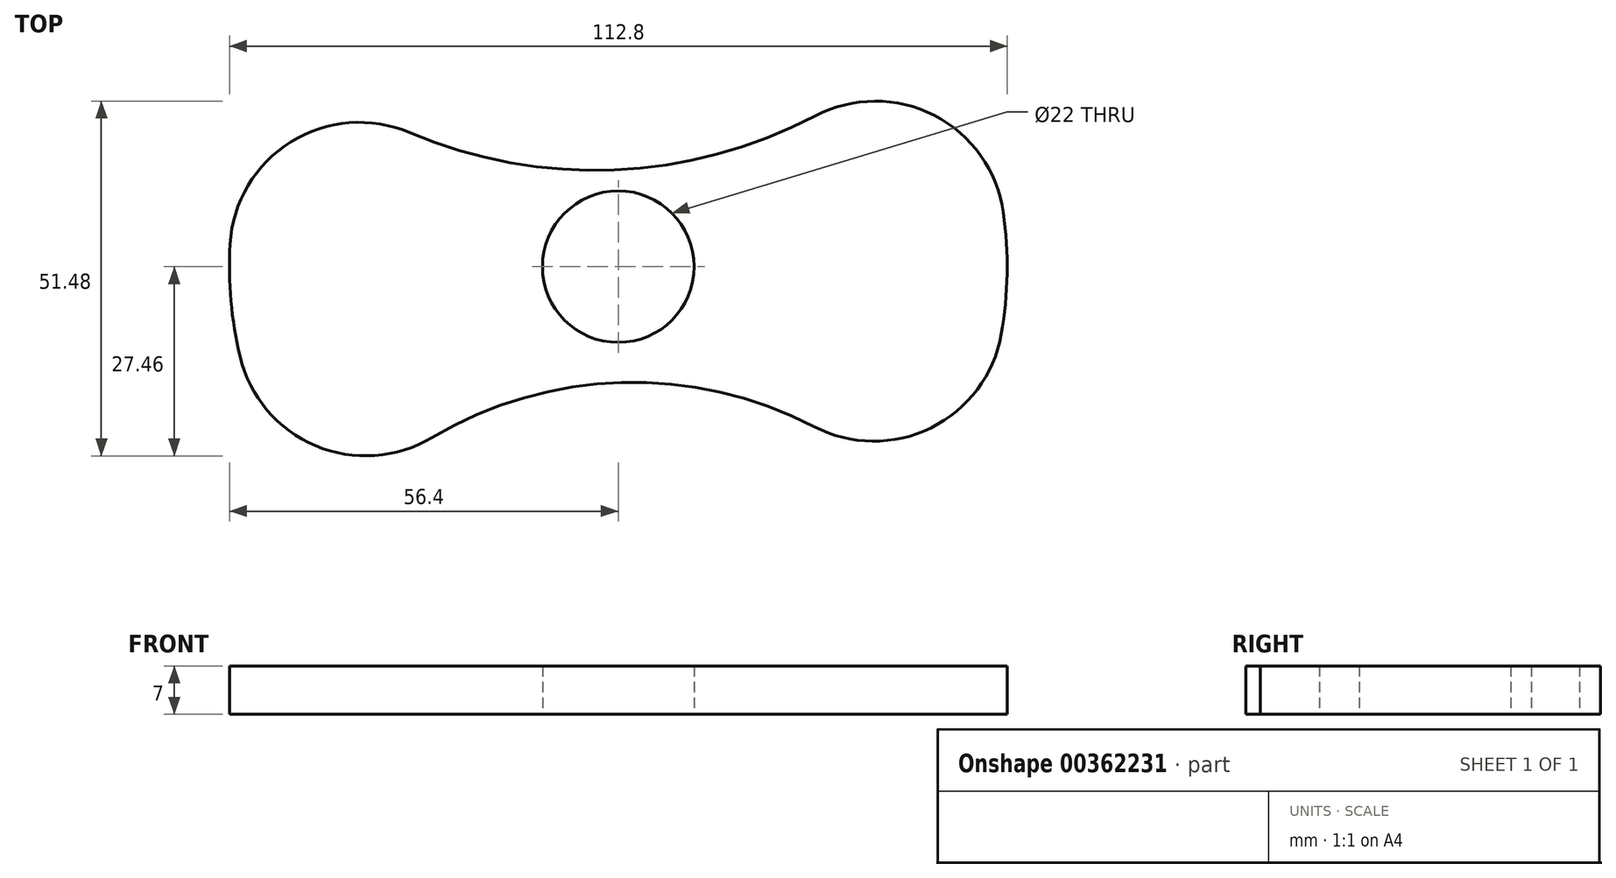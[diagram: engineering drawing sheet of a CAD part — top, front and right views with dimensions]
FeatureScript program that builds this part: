
annotation { "Feature Type Name" : "Feature", "Feature Type Description" : "" }
export const myFeature = defineFeature(function(context is Context, id is Id, definition is map)
    precondition{}
    {
        {
            var Q0;
            Q0=qCreatedBy(makeId("Top.planeOp"),FACE);
            var sketch = newSketch(context, id + "F0", { "sketchPlane" : qUnion([Q0])});
            skCircle(sketch, "E0", {"center": v(0, 0) * mm, "radius": 11 * mm});
            skArc(sketch, "E1", {"start": v(-56.3, 3.26) * mm, "mid": v(-56.18, -4.93) * mm, "end": v(-54.87, -13.02) * mm});
            skPoint(sketch, "E2", {"position": v(-41.94, -37.7) * mm});
            skArc(sketch, "E3.trimOffspring", {"start": v(55.53, -9.84) * mm, "mid": v(56.39, -1) * mm, "end": v(55.85, 7.87) * mm});
            skArc(sketch, "E4", {"start": v(28.39, -23.2) * mm, "mid": v(0.48, -16.8) * mm, "end": v(-27, -24.8) * mm});
            skArc(sketch, "E5", {"start": v(-30.24, 19.45) * mm, "mid": v(-0.58, 14.04) * mm, "end": v(28.54, 21.87) * mm});
            skPoint(sketch, "E6.visualSharp", {"position": v(-47.66, 30.15) * mm});
            skArc(sketch, "E6.filletArc", {"start": v(-30.24, 19.45) * mm, "mid": v(-47.47, 18.12) * mm, "end": v(-56.3, 3.26) * mm});
            skArc(sketch, "E7.filletArc", {"start": v(-54.87, -13.02) * mm, "mid": v(-43.92, -25.97) * mm, "end": v(-27, -24.8) * mm});
            skPoint(sketch, "E8.visualSharp", {"position": v(44.04, -35.23) * mm});
            skArc(sketch, "E8.filletArc", {"start": v(28.39, -23.2) * mm, "mid": v(45.35, -23.4) * mm, "end": v(55.53, -9.84) * mm});
            skPoint(sketch, "E9.visualSharp", {"position": v(45.02, 33.97) * mm});
            skArc(sketch, "E9.filletArc", {"start": v(55.85, 7.87) * mm, "mid": v(45.82, 21.95) * mm, "end": v(28.54, 21.87) * mm});
            skSolve(sketch);
        }
        {
            var Q0;
            Q0=makeQuery(id+"F0.imprint","IMPRINT",FACE,{"disambiguationData":[TD([[makeQuery(id+"F0.imprint","IMPRINT",EDGE,{"derivedFrom":sQuery(id+"F0.wireOp",EDGE,"E0")}),-1.0]])]});
            extrude(context, id + "F1", {"entities" : qUnion([Q0]), "depth" : 7 * mm});
        }
    });
